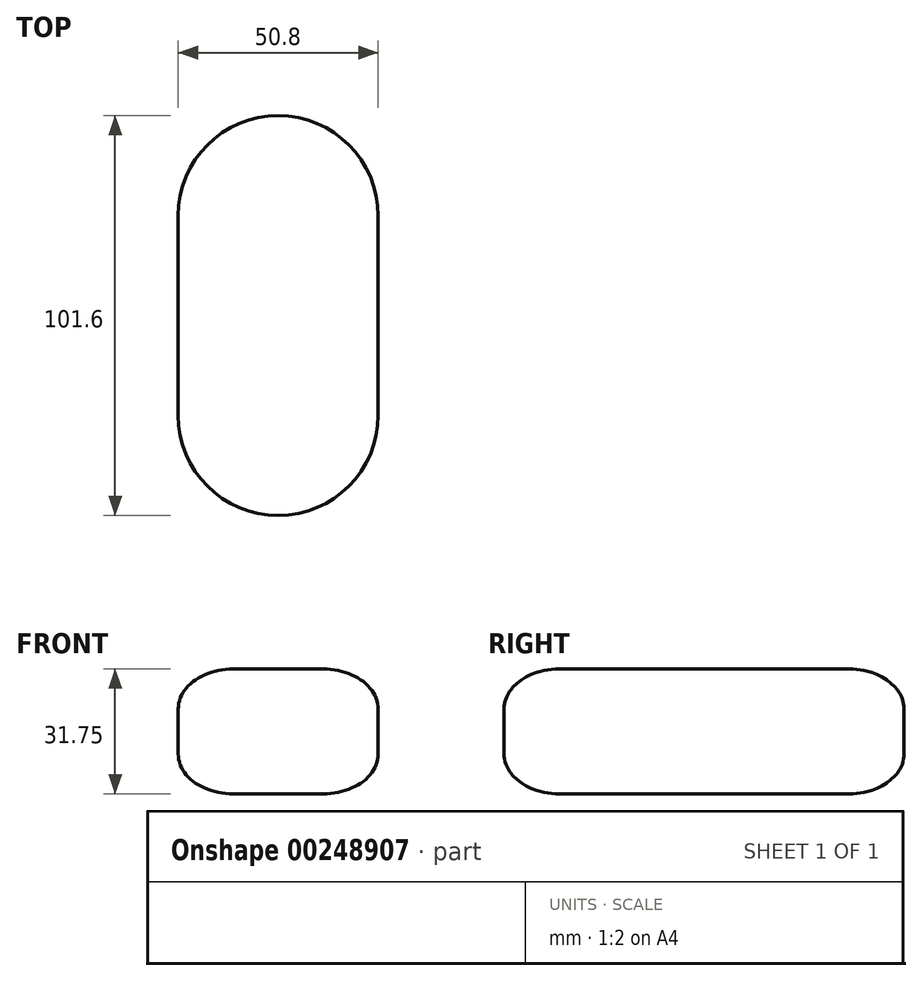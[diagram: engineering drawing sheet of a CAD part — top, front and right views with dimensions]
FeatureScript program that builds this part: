
annotation { "Feature Type Name" : "Feature", "Feature Type Description" : "" }
export const myFeature = defineFeature(function(context is Context, id is Id, definition is map)
    precondition{}
    {
        {
            var Q0;
            Q0=qCreatedBy(makeId("Front.planeOp"),FACE);
            var sketch = newSketch(context, id + "F0", { "sketchPlane" : qUnion([Q0])});
            skLineSegment(sketch, "E0.bottom", {"start": v(0, 0) * mm, "end": v(50.8, 0) * mm});
            skLineSegment(sketch, "E0.top", {"start": v(0, 31.75) * mm, "end": v(50.8, 31.75) * mm});
            skLineSegment(sketch, "E0.left", {"start": v(0, 0) * mm, "end": v(0, 31.75) * mm});
            skLineSegment(sketch, "E0.right", {"start": v(50.8, 0) * mm, "end": v(50.8, 31.75) * mm});
            skSolve(sketch);
        }
        {
            var Q0;
            Q0=makeQuery(id+"F0.imprint","IMPRINT",FACE,{"disambiguationData":[TD([[makeQuery(id+"F0.imprint","IMPRINT",EDGE,{"derivedFrom":sQuery(id+"F0.wireOp",EDGE,"E0.bottom")}),1.0]])]});
            extrude(context, id + "F1", {"entities" : qUnion([Q0]), "oppositeDirection" : true, "depth" : 101.6 * mm});
        }
        {
            var Q0;
            Q0=makeQuery(id+"F1.opExtrude","SWEPT_FACE",FACE,{"disambiguationData":[OSD([sQuery(id+"F0.wireOp",EDGE,"E0.top")])]});
            var sketch = newSketch(context, id + "F2", { "sketchPlane" : qUnion([Q0])});
            skArc(sketch, "E1", {"start": v(50.8, 76.2) * mm, "mid": v(25.4, 101.6) * mm, "end": v(0, 76.2) * mm});
            skPoint(sketch, "E1.first.point", {"position": v(25.4, 101.6) * mm});
            skPoint(sketch, "E1.second.point", {"position": v(50.8, 76.2) * mm});
            skPoint(sketch, "E1.third.point", {"position": v(0, 76.2) * mm});
            skArc(sketch, "E2", {"start": v(0, 25.4) * mm, "mid": v(25.4, 0) * mm, "end": v(50.8, 25.4) * mm});
            skPoint(sketch, "E2.first.point", {"position": v(25.4, 0) * mm});
            skPoint(sketch, "E2.second.point", {"position": v(0, 25.4) * mm});
            skPoint(sketch, "E2.third.point", {"position": v(50.8, 25.4) * mm});
            skLineSegment(sketch, "E3", {"start": v(0, 76.2) * mm, "end": v(0, 25.4) * mm});
            skLineSegment(sketch, "E4", {"start": v(50.8, 76.2) * mm, "end": v(50.8, 25.4) * mm});
            skSolve(sketch);
        }
        {
            var Q0;
            Q0=qCreatedBy(makeId("Front.planeOp"),FACE);
            var Q1;
            Q1=sQuery(id+"F2.wireOp",VERTEX,"E2.center");
            cPlane(context, id + "F3", {"entities" : qUnion([Q0, Q1]), "cplaneType" : CPlaneType.PLANE_POINT, "offset" : 25.4 * mm, "width" : 152.4 * mm, "height" : 152.4 * mm});
        }
        {
            var Q0;
            Q0=qCreatedBy(id+"F3.planeOp",FACE);
            var sketch = newSketch(context, id + "F4", { "sketchPlane" : qUnion([Q0])});
            skLineSegment(sketch, "E5.0.0", {"start": v(50.8, 31.75) * mm, "end": v(0, 31.75) * mm});
            skLineSegment(sketch, "E5.0.1", {"start": v(0, 31.75) * mm, "end": v(0, 0) * mm});
            skLineSegment(sketch, "E5.0.2", {"start": v(0, 0) * mm, "end": v(50.8, 0) * mm});
            skLineSegment(sketch, "E5.0.3", {"start": v(50.8, 0) * mm, "end": v(50.8, 31.75) * mm});
            skEllipticalArc(sketch, "E6", {});
            skPoint(sketch, "E7", {"position": v(36.83, 31.75) * mm});
            skPoint(sketch, "E8", {"position": v(50.8, 21.59) * mm});
            skLineSegment(sketch, "E9.top", {"start": v(36.83, 50.8) * mm, "end": v(76.2, 50.8) * mm});
            skLineSegment(sketch, "E9.left", {"start": v(36.83, 31.75) * mm, "end": v(36.83, 50.8) * mm});
            skLineSegment(sketch, "E9.right", {"start": v(76.2, 21.59) * mm, "end": v(76.2, 50.8) * mm});
            skLineSegment(sketch, "E10", {"start": v(0, 15.87) * mm, "end": v(50.8, 15.87) * mm, "construction": true});
            skLineSegment(sketch, "E11.MirrorCS", {"start": v(36.83, 0) * mm, "end": v(36.83, -19.05) * mm});
            skLineSegment(sketch, "E12.MirrorCS", {"start": v(36.83, -19.05) * mm, "end": v(76.2, -19.05) * mm});
            skLineSegment(sketch, "E13.MirrorCS", {"start": v(76.2, 10.16) * mm, "end": v(76.2, -19.05) * mm});
            skEllipticalArc(sketch, "E14.MirrorCS", {});
            skLineSegment(sketch, "E15", {"start": v(76.2, 21.59) * mm, "end": v(76.2, 10.16) * mm});
            skPoint(sketch, "E16.MirrorCS.end.orphan", {"position": v(76.2, 10.16) * mm});
            skPoint(sketch, "E16.MirrorCS.start.orphan", {"position": v(50.8, 10.16) * mm});
            const initialGuessF4  = {"E6": [0.03683, 0.02159, 1, 0, 0.01397, 0.01016, 0, 1.5707963267948966], "E14.MirrorCS": [0.03683, 0.01016, 1, 0, 0.01397, 0.01016, 4.71238898038469, 0]};
            skSetInitialGuess(sketch, initialGuessF4);
            skSolve(sketch);
        }
        {
            var Q0;
            {var subQ3=sQuery(id+"F4.wireOp",EDGE,"E9.bottom");Q0=makeQuery(id+"F4.imprint","IMPRINT",FACE,{"disambiguationData":[TD([[makeQuery(id+"F4.imprint","IMPRINT",EDGE,{"derivedFrom":subQ3}),1.0]])]});}
            var Q1;
            {var subQ3=sQuery(id+"F4.wireOp",EDGE,"E6");Q1=makeQuery(id+"F4.imprint","IMPRINT",FACE,{"disambiguationData":[TD([[makeQuery(id+"F4.imprint","IMPRINT",EDGE,{"derivedFrom":subQ3}),-1.0]])]});}
            var Q2;
            {var subQ3=sQuery(id+"F4.wireOp",EDGE,"E14.MirrorCS");Q2=makeQuery(id+"F4.imprint","IMPRINT",FACE,{"disambiguationData":[TD([[makeQuery(id+"F4.imprint","IMPRINT",EDGE,{"derivedFrom":subQ3}),-1.0]])]});}
            var Q3;
            {var subQ1=sQuery(id+"F4.wireOp",EDGE,"E11.MirrorCS");Q3=makeQuery(id+"F4.imprint","IMPRINT",FACE,{"disambiguationData":[TD([[makeQuery(id+"F4.imprint","IMPRINT",EDGE,{"derivedFrom":subQ1}),1.0]])]});}
            var Q4;
            Q4=sQuery(id+"F2.wireOp",EDGE,"E4");
            var Q5;
            Q5=sQuery(id+"F2.wireOp",EDGE,"E1");
            var Q6;
            Q6=sQuery(id+"F2.wireOp",EDGE,"E3");
            var Q7;
            Q7=sQuery(id+"F2.wireOp",EDGE,"E2");
            sweep(context, id + "F5", {"operationType" : NewBodyOperationType.REMOVE, "profiles" : qUnion([Q0, Q1, Q2, Q3]), "path" : qUnion([Q4, Q5, Q6, Q7])});
        }
        {
            var Q0;
            Q0=qCreatedBy(makeId("Front.planeOp"),FACE);
            var sketch = newSketch(context, id + "F6", { "sketchPlane" : qUnion([Q0])});
            skLineSegment(sketch, "E17.0.0", {"start": v(0, 21.59) * mm, "end": v(50.8, 21.59) * mm});
            skEllipticalArc(sketch, "E17.0.1", {});
            skLineSegment(sketch, "E17.0.2", {"start": v(36.83, 31.75) * mm, "end": v(13.97, 31.75) * mm});
            skEllipticalArc(sketch, "E17.0.3", {});
            skLineSegment(sketch, "E18", {"start": v(1.28, 25.84) * mm, "end": v(8.9, 25.84) * mm});
            skLineSegment(sketch, "E19", {"start": v(8.9, 25.84) * mm, "end": v(6.45, 23.35) * mm});
            skLineSegment(sketch, "E20", {"start": v(6.45, 23.35) * mm, "end": v(44.43, 23.35) * mm});
            skLineSegment(sketch, "E21", {"start": v(44.43, 23.35) * mm, "end": v(41.9, 25.84) * mm});
            skLineSegment(sketch, "E22", {"start": v(41.9, 25.84) * mm, "end": v(49.52, 25.84) * mm});
            const initialGuessF6  = {"E17.0.1": [0.03683, 0.02159, 1, 0, 0.01397, 0.01016, 0, 1.5707963267948966], "E17.0.3": [0.01397, 0.02159, -1, 0, 0.01397, 0.01016, 4.71238898038469, 0]};
            skSetInitialGuess(sketch, initialGuessF6);
            skSolve(sketch);
        }
        {
            var Q0;
            Q0=sQuery(id+"F6.wireOp",EDGE,"E18");
            var Q1;
            Q1=sQuery(id+"F6.wireOp",EDGE,"E19");
            var Q2;
            Q2=sQuery(id+"F6.wireOp",EDGE,"E20");
            var Q3;
            Q3=sQuery(id+"F6.wireOp",EDGE,"E22");
            var Q4;
            Q4=sQuery(id+"F6.wireOp",EDGE,"E21");
            var Q5;
            Q5=makeQuery(id+"F5.boolean.opBoolean","COPY",VERTEX,{"derivedFrom":makeQuery(id+"F5.opSweep","MID_CAP_VERTEX",VERTEX,{"disambiguationData":[OSD([sQuery(id+"F2.wireOp",EDGE,"E4"),sQuery(id+"F4.wireOp",EDGE,"E5.0.3"),sQuery(id+"F4.wireOp",EDGE,"E6")])],"capPos":3.0})});
            extrude(context, id + "F7", {"bodyType" : ToolBodyType.SURFACE, "surfaceEntities" : qUnion([Q0, Q1, Q2, Q3, Q4]), "endBound" : BoundingType.UP_TO_VERTEX, "oppositeDirection" : true, "endBoundEntityVertex" : qUnion([Q5]), "depth" : 25.4 * mm});
        }
        {
            var Q0;
            Q0=makeQuery(id+"F7.opExtrude","CAP_VERTEX",VERTEX,{"disambiguationData":[OSD([sQuery(id+"F6.wireOp",VERTEX,"E20.start"),sQuery(id+"F6.wireOp",EDGE,"E19"),sQuery(id+"F6.wireOp",EDGE,"E20")])],"isStart":true});
            var Q1;
            Q1=makeQuery(id+"F7.opExtrude","CAP_VERTEX",VERTEX,{"disambiguationData":[OSD([sQuery(id+"F6.wireOp",VERTEX,"E21.start"),sQuery(id+"F6.wireOp",EDGE,"E20"),sQuery(id+"F6.wireOp",EDGE,"E21")])],"isStart":true});
            var Q2;
            Q2=makeQuery(id+"F7.opExtrude","CAP_VERTEX",VERTEX,{"disambiguationData":[OSD([sQuery(id+"F6.wireOp",VERTEX,"E21.end"),sQuery(id+"F6.wireOp",EDGE,"E21"),sQuery(id+"F6.wireOp",EDGE,"E22")])],"isStart":true});
            cPlane(context, id + "F8", {"entities" : qUnion([Q0, Q1, Q2]), "cplaneType" : CPlaneType.THREE_POINT, "offset" : 25.4 * mm, "width" : 152.4 * mm, "height" : 152.4 * mm});
        }
        {
            var Q0;
            Q0=qCreatedBy(id+"F8.planeOp",FACE);
            var sketch = newSketch(context, id + "F9", { "sketchPlane" : qUnion([Q0])});
            skPoint(sketch, "E23.0", {"position": v(-8.9, 25.84) * mm});
            skPoint(sketch, "E24.0", {"position": v(-6.45, 23.35) * mm});
            skPoint(sketch, "E25.0", {"position": v(-44.43, 23.35) * mm});
            skPoint(sketch, "E26.0", {"position": v(-41.9, 25.84) * mm});
            skLineSegment(sketch, "E27", {"start": v(-41.9, 25.84) * mm, "end": v(-44.43, 23.35) * mm});
            skLineSegment(sketch, "E28", {"start": v(-6.45, 23.35) * mm, "end": v(-44.43, 23.35) * mm});
            skLineSegment(sketch, "E29", {"start": v(-6.45, 23.35) * mm, "end": v(-8.9, 25.84) * mm});
            skLineSegment(sketch, "E30", {"start": v(-8.9, 25.84) * mm, "end": v(-41.9, 25.84) * mm});
            skSolve(sketch);
        }
        {
            var Q0;
            Q0=sQuery(id+"F9.wireOp",EDGE,"E28");
            var Q1;
            Q1=sQuery(id+"F9.wireOp",EDGE,"E30");
            var Q2;
            Q2=sQuery(id+"F9.wireOp",EDGE,"E29");
            loft(context, id + "F10", {"bodyType" : ToolBodyType.SURFACE, "wireProfilesArray" : [{ "wireProfileEntities" : qUnion([Q0]) }, { "wireProfileEntities" : qUnion([Q1]) }], "guidesArray" : [{ "guideEntities" : qUnion([Q2]), "guideDerivativeType" : LoftGuideDerivativeType.DEFAULT, "guideDerivativeMagnitude" : 1 }]});
        }
    });
